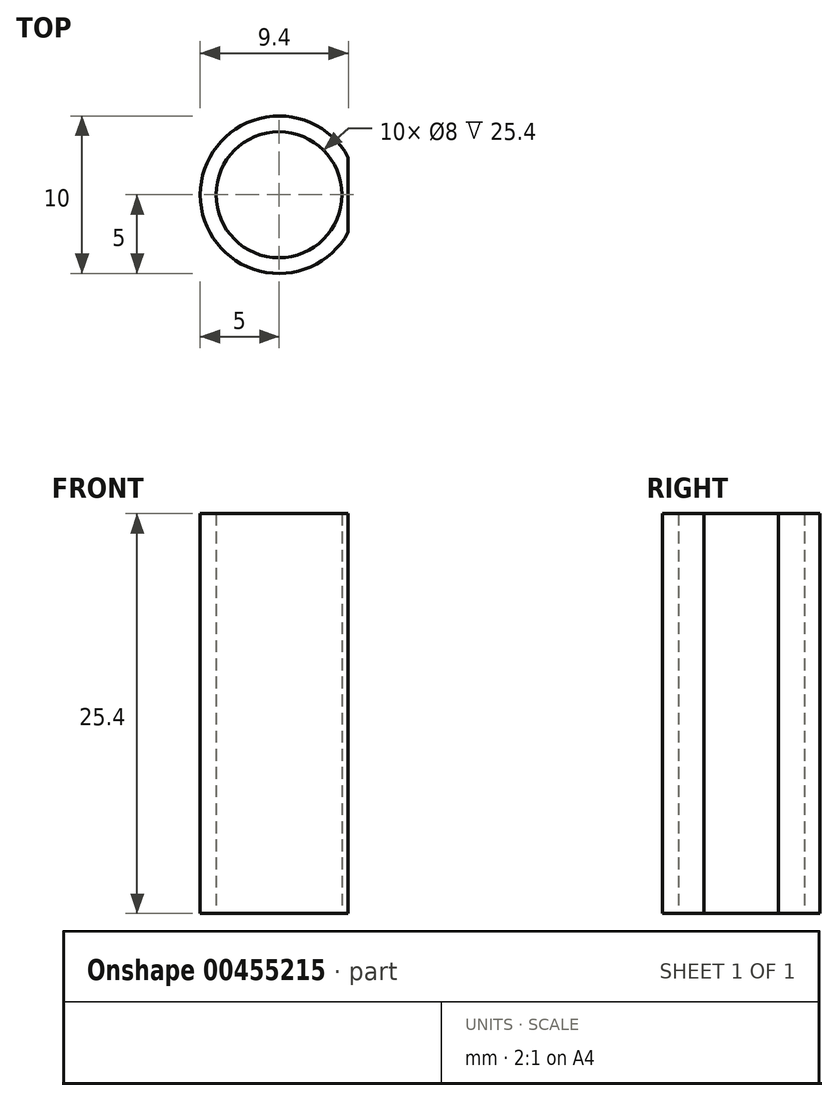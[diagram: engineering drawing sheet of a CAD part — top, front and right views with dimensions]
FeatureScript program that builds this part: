
annotation { "Feature Type Name" : "Feature", "Feature Type Description" : "" }
export const myFeature = defineFeature(function(context is Context, id is Id, definition is map)
    precondition{}
    {
        {
            var Q0;
            Q0=qCreatedBy(makeId("Top.planeOp"),FACE);
            var sketch = newSketch(context, id + "F0", { "sketchPlane" : qUnion([Q0])});
            skCircle(sketch, "E0", {"center": v(0, 0) * mm, "radius": 5 * mm});
            skSolve(sketch);
        }
        {
            var Q0;
            Q0=makeQuery(id+"F0.imprint","IMPRINT",FACE,{"disambiguationData":[TD([[makeQuery(id+"F0.imprint","IMPRINT",EDGE,{"derivedFrom":sQuery(id+"F0.wireOp",EDGE,"E0")}),1.0]])]});
            extrude(context, id + "F1", {"entities" : qUnion([Q0]), "depth" : 25.4 * mm});
        }
        {
            var Q0;
            Q0=makeQuery(id+"F1.opExtrude","CAP_FACE",FACE,{"disambiguationData":[OSD([sQuery(id+"F0.wireOp",EDGE,"E0")])],"isStart":false});
            var Q1;
            Q1=makeQuery(id+"F1.opExtrude","CAP_FACE",FACE,{"disambiguationData":[OSD([sQuery(id+"F0.wireOp",EDGE,"E0")])],"isStart":true});
            var Q2;
            Q2=makeQuery(id+"F1.opExtrude","SWEPT_BODY",BODY,{"disambiguationData":[OSD([sQuery(id+"F0.wireOp",EDGE,"E0")])]});
            shell(context, id + "F2", {"entities" : qUnion([Q0, Q1]), "parts" : qUnion([Q2]), "thickness" : 1 * mm});
        }
        {
            var Q0;
            Q0=qCreatedBy(makeId("Top.planeOp"),FACE);
            var sketch = newSketch(context, id + "F3", { "sketchPlane" : qUnion([Q0])});
            skCircle(sketch, "E1.0.0", {"center": v(0, 0) * mm, "radius": 5 * mm});
            skLineSegment(sketch, "E2", {"start": v(4.4, -2.38) * mm, "end": v(4.4, 2.38) * mm});
            skSolve(sketch);
        }
        {
            var Q0;
            {var subQ0=sQuery(id+"F3.wireOp",EDGE,"E2");Q0=makeQuery(id+"F3.imprint","IMPRINT",FACE,{"disambiguationData":[TD([[makeQuery(id+"F3.imprint","IMPRINT",EDGE,{"derivedFrom":subQ0}),-1.0]])]});}
            extrude(context, id + "F4", {"entities" : qUnion([Q0]), "operationType" : NewBodyOperationType.REMOVE, "depth" : 25.4 * mm});
        }
        {
            var Q0;
            Q0=qCreatedBy(makeId("Top.planeOp"),FACE);
            cPlane(context, id + "F5", {"entities" : qUnion([Q0]), "cplaneType" : CPlaneType.OFFSET, "offset" : 25 * mm, "oppositeDirection" : true, "width" : 150 * mm, "height" : 150 * mm});
        }
    });
